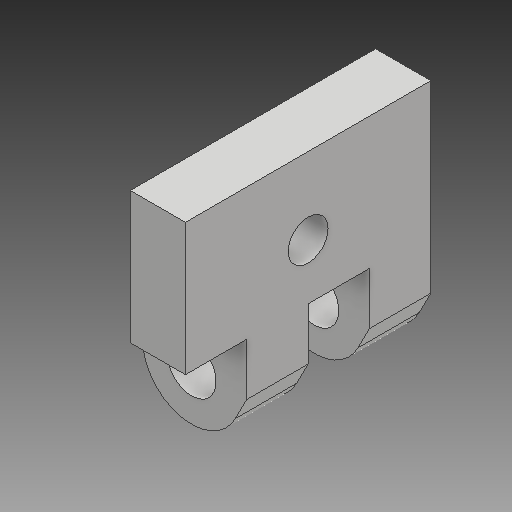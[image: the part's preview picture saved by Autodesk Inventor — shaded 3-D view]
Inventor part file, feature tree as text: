
AUTODESK INVENTOR PART (.ipt)
format: ipt  version: 2018 (Build 220112000, 112)  size: 146,432 bytes
history: native  units: mm
features: sketch x3, extrude x2, projected_geometry x2, hole x1
ambient origin geometry x8: Origin, YZ Plane, XZ Plane, XY Plane, X Axis, Y Axis, Z Axis, Center Point
bodies: Volumenkörper1 (feature_tree)
feature tree (8):
  extrude  "Extrusion1"  Depth=0.8mm
  extrude  "Extrusion2"  Depth=3.0mm
  hole  "Bohrung2"  [1 undecoded]
  sketch  "Skizze1"  dims[d0=0.9mm d2=0.8mm]
  sketch  "Skizze2"  dims[d3=1.6mm d4=3.0mm]
  projected_geometry  "Projizierte Kontur1"
  sketch  "Skizze4"  dims[d5=4.0mm d6=0.0mm d7=0.85mm d8=2.0mm d9=1.0mm d10=1.0mm d11=1.0mm d12=4.0mm d13=0.0mm d22=1.25mm d23=0.65mm d24=6.0mm d25=1.0mm d26=2.0mm d27=90.0deg d28=8.0mm d29=20.594885mm]
  projected_geometry  "Projizierte Kontur3"
note: 1 required parameter value undecoded (feature->parameter linkage not recoverable at this tier; creation-order binding heuristic only, values carry confidence <= 0.55)
